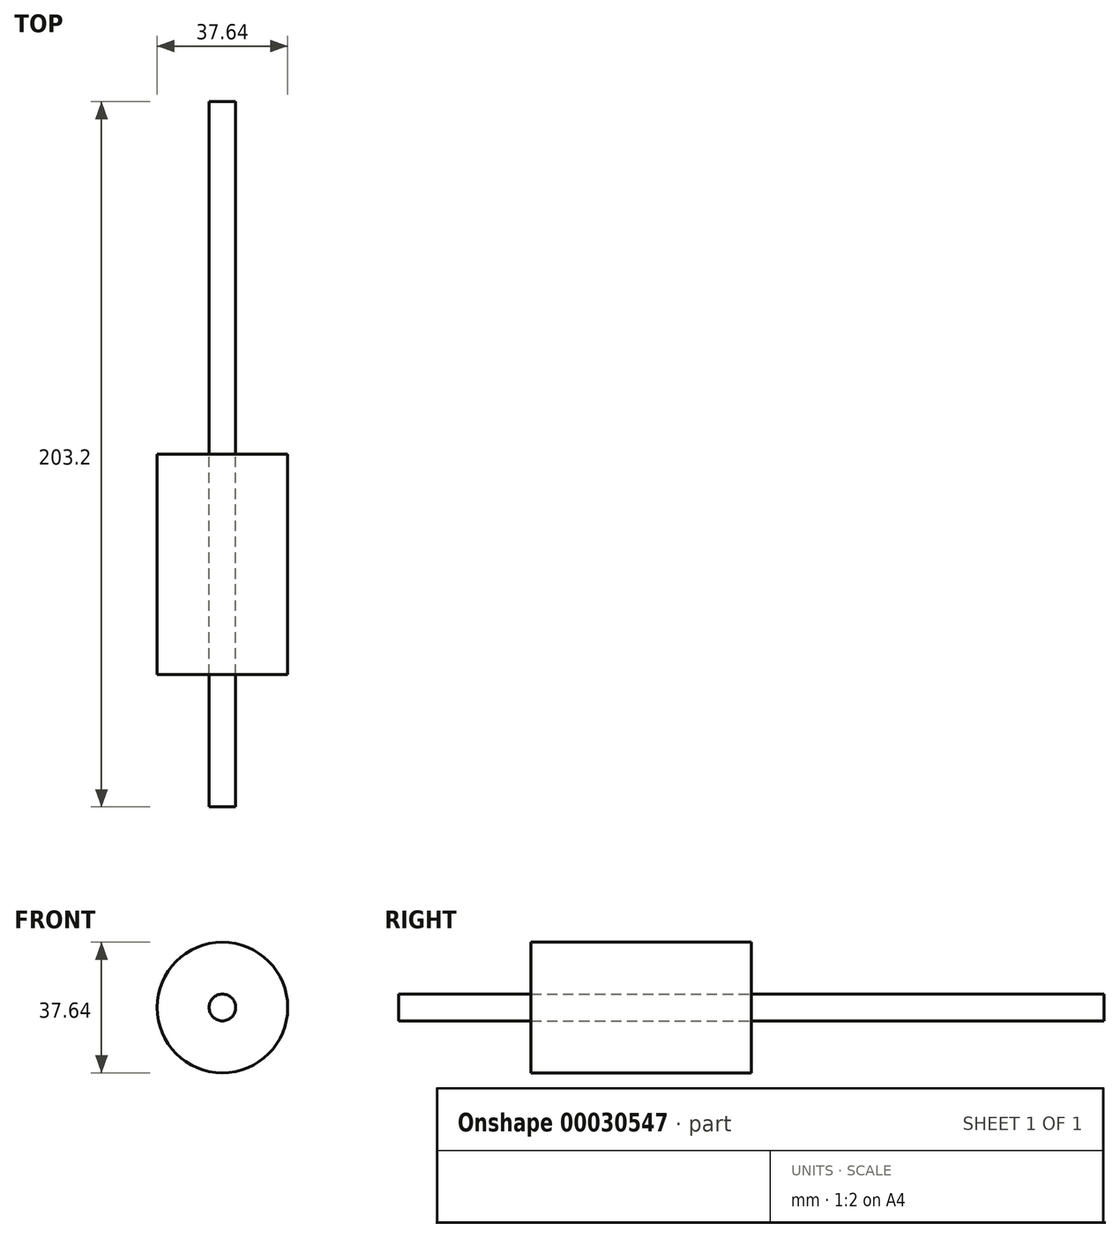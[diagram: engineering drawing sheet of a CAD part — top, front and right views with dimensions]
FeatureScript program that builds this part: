
annotation { "Feature Type Name" : "Feature", "Feature Type Description" : "" }
export const myFeature = defineFeature(function(context is Context, id is Id, definition is map)
    precondition{}
    {
        {
            var Q0;
            Q0=qCreatedBy(makeId("Right.planeOp"),FACE);
            var sketch = newSketch(context, id + "F0", { "sketchPlane" : qUnion([Q0])});
            skLineSegment(sketch, "E0", {"start": v(47.7, 32.67) * mm, "end": v(47.7, -30.72) * mm});
            skLineSegment(sketch, "E1.bottom", {"start": v(47.7, -30.72) * mm, "end": v(-12.8, -30.72) * mm});
            skLineSegment(sketch, "E1.top", {"start": v(47.7, 24.12) * mm, "end": v(-12.8, 24.12) * mm});
            skLineSegment(sketch, "E1.left", {"start": v(47.7, -30.72) * mm, "end": v(47.7, 24.12) * mm});
            skLineSegment(sketch, "E1.right", {"start": v(-12.8, -30.72) * mm, "end": v(-12.8, 24.12) * mm});
            skSolve(sketch);
        }
        {
            var Q0;
            Q0=qCreatedBy(makeId("Front.planeOp"),FACE);
            var sketch = newSketch(context, id + "F1", { "sketchPlane" : qUnion([Q0])});
            skCircle(sketch, "E2", {"center": v(0, 0) * mm, "radius": 3.84 * mm});
            skSolve(sketch);
        }
        {
            var Q0;
            Q0=makeQuery(id+"F1.imprint","IMPRINT",FACE,{"disambiguationData":[TD([[makeQuery(id+"F1.imprint","IMPRINT",EDGE,{"derivedFrom":sQuery(id+"F1.wireOp",EDGE,"E2")}),1.0]])]});
            extrude(context, id + "F2", {"entities" : qUnion([Q0]), "endBound" : BoundingType.SYMMETRIC, "depth" : 203.2 * mm});
        }
        {
            var Q0;
            Q0=sQuery(id+"F0.wireOp",EDGE,"E1.top");
            var Q1;
            Q1=sQuery(id+"F0.wireOp",EDGE,"E1.bottom");
            var Q2;
            Q2=makeQuery(id+"F2.opExtrude","CAP_EDGE",EDGE,{"disambiguationData":[OSD([sQuery(id+"F1.wireOp",EDGE,"E2")])],"isStart":true});
            revolve(context, id + "F3", {"bodyType" : ToolBodyType.SURFACE, "surfaceEntities" : qUnion([Q0, Q1]), "axis" : qUnion([Q2]), "revolveType" : RevolveType.ONE_DIRECTION, "angle" : 184.34 * degree});
        }
        {
            var Q0;
            Q0=qCreatedBy(makeId("Front.planeOp"),FACE);
            var sketch = newSketch(context, id + "F4", { "sketchPlane" : qUnion([Q0])});
            skCircle(sketch, "E3", {"center": v(0, 0) * mm, "radius": 18.82 * mm});
            skSolve(sketch);
        }
        {
            var Q0;
            Q0 = qSketchRegion(id + "F4", true);
            extrude(context, id + "F5", {"entities" : qUnion([Q0]), "depth" : 63.5 * mm});
        }
    });
